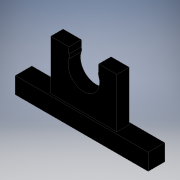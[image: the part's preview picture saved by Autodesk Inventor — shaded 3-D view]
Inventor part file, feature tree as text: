
AUTODESK INVENTOR PART (.ipt)
format: ipt  version: 2017 (Build 210142000, 142)  size: 139,776 bytes
history: native  units: in
note: dims shown in document units (in); Inventor stores cm internally (conversion verified against a paired STEP export)
features: extrude x5, sketch x5, fillet x2
ambient origin geometry x8: Origin, YZ Plane, XZ Plane, XY Plane, X Axis, Y Axis, Z Axis, Center Point
bodies: Solid1 (feature_tree)
feature tree (12):
  extrude  "Extrusion1"  Depth=0.7874in
  extrude  "Extrusion2"  Depth=3.1496in
  extrude  "Extrusion3"  Depth=2.3622in TaperAngle=0.0deg
  extrude  "Extrusion4"  Depth=0.748in
  extrude  "Extrusion5"  Depth=0.3in
  fillet  "Fillet1"  Radius=0.7071in
  fillet  "Fillet2"  Radius=0.5906in
  sketch  "Sketch1"  dims[d0=6.3181in d1=0.7874in]
  sketch  "Sketch2"  dims[d2=0.7874in d3=0.0in d4=3.1496in]
  sketch  "Sketch3"  dims[d5=0.5906in d6=2.3622in d7=0.0in]
  sketch  "Sketch4"  dims[d8=1.4961in d9=0.748in]
  sketch  "Sketch5"  dims[d10=0.5906in d11=0.0in d12=0.2981in d13=0.7071in d14=0.5906in d15=0.0in d16=0.707in d17=0.1094in d18=0.2981in d19=0.5906in d20=0.0in d21=0.3in d22=0.3in]
